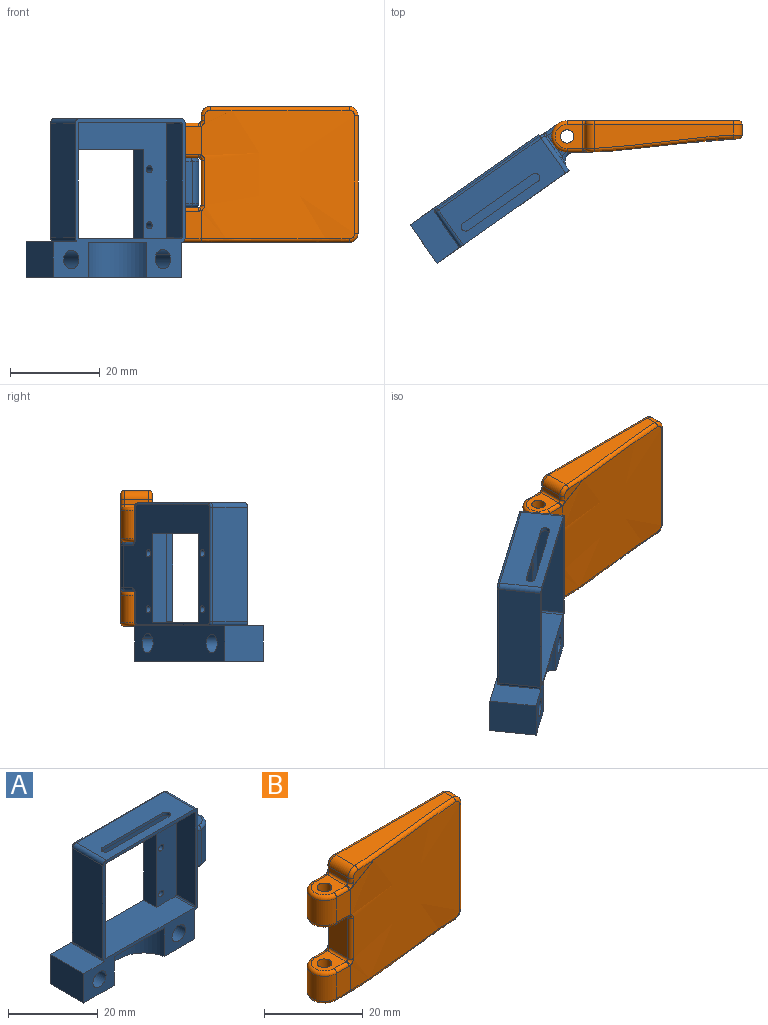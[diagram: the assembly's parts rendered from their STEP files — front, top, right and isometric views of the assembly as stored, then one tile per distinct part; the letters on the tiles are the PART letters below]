
ASSEMBLY  parts=2 mates=1
PART A: 71 faces, bbox 43.8x11x35.5 mm
  f0: plane 15.72x6.5mm, normal (0,0,-1), area 76.7mm2, adj f17,f61
  f1: plane 18x4mm, normal (0,0,-1), area 72mm2, adj f2,f7,f8,f9
  f2: plane 20x4mm, normal (-1,0,0), area 80mm2, adj f1,f8,f9,f13
  f3: cylinder r=0.8mm len=4mm, axis (0,1,0), area 20.1mm2, adj f8,f9
  f4: cylinder r=0.8mm len=4mm, axis (0,1,0), area 20.1mm2, adj f8,f9
  f5: cylinder r=0.8mm len=4mm, axis (0,1,0), area 20.1mm2, adj f8,f9
  f6: cylinder r=0.8mm len=4mm, axis (0,1,0), area 20.1mm2, adj f8,f9
  f7: plane 20x4mm, normal (1,0,0), area 80mm2, adj f1,f8,f9,f13
  f8: plane 28.3x26mm, normal (0,-1,0), area 367.7mm2, adj f1,f2,f3,f4,f5,f6,f7,f10
  f9: plane 33.4x26.6mm, normal (0,1,0), area 443.5mm2, adj f1,f2,f3,f4,f5,f6,f7,f13
  f10: plane 25.3x6mm, normal (-1,0,0), area 151.8mm2, adj f8,f17,f28,f29
  f11: plane 27.6x6mm, normal (0,0,-1), area 124.5mm2, adj f8,f17,f18,f19,f20,f21,f27,f28
  f12: plane 25.3x6mm, normal (1,0,0), area 151.8mm2, adj f8,f17,f26,f27
  f13: plane 27.6x10mm, normal (0,0,1), area 237.6mm2, adj f2,f7,f8,f9,f17,f26,f29
  f14: plane 25.6x9.5mm, normal (1,0,0), area 143.4mm2, adj f17,f22,f25,f35,f44,f45,f46,f47
  f15: plane 27.9x9.5mm, normal (0,0,1), area 223.9mm2, adj f17,f18,f19,f20,f21,f22,f23,f53
  f16: plane 25.6x9.5mm, normal (-1,0,0), area 243.2mm2, adj f17,f23,f24,f55
  f17: plane 35.98x35.43mm, normal (0,-1,0), area 213.2mm2, adj f0,f10,f11,f12,f13,f14,f15,f16
  f18: plane 19x0.8mm, normal (0,-1,0), area 15.2mm2, adj f11,f15,f20,f21
  f19: plane 19x0.8mm, normal (0,1,0), area 15.2mm2, adj f11,f15,f20,f21
  f20: cylinder r=1mm len=2mm, axis (0,0,-1), area 2.5mm2, adj f11,f15,f18,f19
  f21: cylinder r=1mm len=2mm, axis (0,0,1), area 2.5mm2, adj f11,f15,f18,f19
  f22: cylinder r=1mm len=9.5mm, axis (0,1,0), area 14.9mm2, adj f14,f15,f17,f52
  f23: cylinder r=1mm len=9.5mm, axis (0,-1,0), area 14.9mm2, adj f15,f16,f17,f54
  f24: cylinder r=1mm len=9.5mm, axis (0,1,0), area 9.3mm2, adj f16,f17,f56,f70
  f25: cylinder r=1mm len=9.5mm, axis (0,-1,0), area 14.7mm2, adj f14,f17,f58,f68
  f26: cylinder r=0.35mm len=6mm, axis (0,-1,0), area 3.3mm2, adj f8,f12,f13,f17
  f27: cylinder r=0.35mm len=6mm, axis (0,1,0), area 3.3mm2, adj f8,f11,f12,f17
  f28: cylinder r=0.35mm len=6mm, axis (0,-1,0), area 3.3mm2, adj f8,f10,f11,f17
  f29: cylinder r=0.35mm len=6mm, axis (0,1,0), area 3.3mm2, adj f8,f10,f13,f17
  f30: plane 9.4x2mm, normal (0,-1,0), area 18.8mm2, adj f31,f35,f37,f41
  f31: cylinder r=3.5mm len=9.4mm, axis (0,0,-1), area 103.4mm2, adj f9,f30,f38,f42
  f32: cylinder r=1.5mm len=11mm, axis (0,0,-1), area 103.7mm2, adj f33,f34
  f33: plane 6.2x5.84mm, normal (0,0,1), area 23.5mm2, adj f32,f40,f41,f42,f43,f45
  f34: plane 6.2x5.84mm, normal (0,0,-1), area 23.5mm2, adj f32,f36,f37,f38,f39,f48
  f35: cylinder r=2mm len=9.4mm, axis (0,0,1), area 29.5mm2, adj f14,f30,f36,f40
  f36: torus R=2.8mm, axis (0,0,1), area 2.7mm2, adj f34,f35,f37,f47
  f37: cylinder r=0.8mm len=2mm, axis (1,0,0), area 2.5mm2, adj f30,f34,f36,f38
  f38: torus R=2.7mm, axis (0,0,1), area 12.7mm2, adj f31,f34,f37,f39
  f39: cylinder r=0.8mm len=3.5mm, axis (-1,0,0), area 4.4mm2, adj f9,f34,f38,f49
  f40: torus R=2.8mm, axis (0,0,1), area 2.7mm2, adj f33,f35,f41,f44
  f41: cylinder r=0.8mm len=2mm, axis (-1,0,0), area 2.5mm2, adj f30,f33,f40,f42
  f42: torus R=2.7mm, axis (0,0,1), area 12.7mm2, adj f31,f33,f41,f43
  f43: cylinder r=0.8mm len=3.5mm, axis (1,0,0), area 4.4mm2, adj f9,f33,f42,f46
  f44: bspline ~2.36x1.3mm, area 1.1mm2, adj f14,f40,f45
  f45: cylinder r=0.5mm len=5.84mm, axis (0,1,0), area 4.6mm2, adj f14,f33,f44,f46
  f46: torus R=1.3mm, axis (1,0,0), area 0.5mm2, adj f14,f43,f45,f50
  f47: bspline ~2.73x1.3mm, area 1.1mm2, adj f14,f36,f48
  f48: cylinder r=0.5mm len=5.84mm, axis (0,-1,0), area 4.6mm2, adj f14,f34,f47,f49
  f49: torus R=1.3mm, axis (1,0,0), area 0.5mm2, adj f14,f39,f48,f60
  f50: bspline ~1.48x1mm, area 0.7mm2, adj f9,f46,f51
  f51: cylinder r=0.5mm len=7.34mm, axis (0,0,1), area 5.8mm2, adj f9,f14,f50,f52
  f52: torus R=0.5mm, axis (0,-1,0), area 1mm2, adj f9,f22,f51,f53
  f53: cylinder r=0.5mm len=27.9mm, axis (-1,0,0), area 21.9mm2, adj f9,f15,f52,f54
  f54: torus R=0.5mm, axis (0,-1,0), area 1mm2, adj f9,f23,f53,f55
  f55: cylinder r=0.5mm len=25.6mm, axis (0,0,-1), area 20.1mm2, adj f9,f16,f54,f56
  f56: torus R=0.5mm, axis (0,-1,0), area 0.8mm2, adj f9,f24,f55,f57,f70
  f57: cylinder r=0.5mm len=27.9mm, axis (1,0,0), area 10mm2, adj f9,f56,f58,f70
  f58: torus R=0.5mm, axis (0,-1,0), area 1mm2, adj f9,f25,f57,f59,f68,f70
  f59: cylinder r=0.5mm len=6.34mm, axis (0,0,1), area 5mm2, adj f9,f14,f58,f60
  f60: bspline ~1.48x1mm, area 0.7mm2, adj f9,f49,f59
  f61: cylinder r=8mm len=15.72mm, axis (0,0,1), area 173.1mm2, adj f0,f17,f67
  f62: cylinder r=2.09mm len=10.5mm, axis (0,-1,0), area 79.3mm2, adj f17,f63,f64
  f63: cylinder r=2.06mm len=10.5mm, axis (0,1,0), area 60.9mm2, adj f17,f62,f64
  f64: plane 35x8mm, normal (0,1,0), area 252.4mm2, adj f62,f63,f65,f66,f67,f68,f69,f70
  f65: cylinder r=2mm len=10.5mm, axis (0,1,0), area 37mm2, adj f17,f64,f66
  f66: cylinder r=2.06mm len=10.5mm, axis (0,1,0), area 99.4mm2, adj f17,f64,f65
  f67: plane 35x10.5mm, normal (0,0,-1), area 290.8mm2, adj f17,f61,f64,f68,f69
  f68: plane 10.5x8mm, normal (1,0,0), area 82.3mm2, adj f17,f25,f58,f64,f67,f70
  f69: plane 10.5x8mm, normal (-1,0,0), area 84mm2, adj f17,f64,f67,f70
  f70: plane 35x10.5mm, normal (0,0,1), area 86.3mm2, adj f17,f24,f56,f57,f58,f64,f68,f69
PART B: 58 faces, bbox 43x7.6x30.6 mm
  f0: plane 6.28x4mm, normal (0,-1,0), area 24.7mm2, adj f3,f10,f34,f35,f39
  f1: cylinder r=1.5mm len=7.78mm, axis (0,0,-1), area 73.3mm2, adj f8,f15
  f2: plane 38.2x28.7mm, normal (0,1,0), area 1018mm2, adj f3,f4,f22,f24,f26,f28,f30,f36
  f3: cylinder r=3.5mm len=7mm, axis (0,0,-1), area 67.9mm2, adj f0,f2,f32,f37
  f4: cylinder r=3.5mm len=7mm, axis (0,0,-1), area 67.9mm2, adj f2,f5,f23,f54
  f5: plane 6.38x4mm, normal (0,-1,0), area 24.7mm2, adj f4,f10,f25,f27,f56,f57
  f6: cylinder r=1.5mm len=7.78mm, axis (0,0,-1), area 73.3mm2, adj f7,f14
  f7: plane 6.2x5.4mm, normal (0,0,1), area 23.3mm2, adj f6,f18,f52,f54,f56
  f8: plane 39.7x5.4mm, normal (0,0,-1), area 157.5mm2, adj f1,f19,f36,f37,f39,f41
  f9: plane 5.4x1.2mm, normal (-1,0,0), area 6.5mm2, adj f18,f20,f48,f53
  f10: extruded ~34.21x28.7mm, area 972.4mm2, adj f0,f5,f29,f31,f33,f41,f43,f45
  f11: plane 26.3x2.4mm, normal (1,0,0), area 63.2mm2, adj f19,f21,f40,f45
  f12: plane 31x5.37mm, normal (0,0,1), area 120.8mm2, adj f20,f21,f44,f49
  f13: plane 10.05x5.4mm, normal (-1,0,0), area 54.2mm2, adj f16,f17,f26,f31
  f14: plane 6.2x5.4mm, normal (0,0,-1), area 23.3mm2, adj f6,f17,f22,f23,f25
  f15: plane 6.2x5.4mm, normal (0,0,1), area 23.3mm2, adj f1,f16,f30,f32,f34
  f16: cylinder r=0.5mm len=5.4mm, axis (0,-1,0), area 4.2mm2, adj f13,f15,f28,f33,f35
  f17: cylinder r=0.5mm len=5.4mm, axis (0,1,0), area 4.2mm2, adj f13,f14,f24,f27,f29
  f18: cylinder r=0.5mm len=5.4mm, axis (0,1,0), area 4.2mm2, adj f7,f9,f50,f55,f57
  f19: cylinder r=2mm len=2.43mm, axis (0,1,0), area 7.6mm2, adj f8,f11,f38,f43
  f20: cylinder r=2mm len=5.4mm, axis (0,1,0), area 16.9mm2, adj f9,f12,f46,f51
  f21: cylinder r=2mm len=2.43mm, axis (0,-1,0), area 7.6mm2, adj f11,f12,f42,f47
  f22: cylinder r=0.8mm len=3.5mm, axis (-1,0,0), area 4.4mm2, adj f2,f14,f23,f24
  f23: torus R=2.7mm, axis (0,0,1), area 12.7mm2, adj f4,f14,f22,f25
  f24: torus R=1.3mm, axis (0,1,0), area 1.6mm2, adj f2,f17,f22,f26
  f25: cylinder r=0.8mm len=3.5mm, axis (1,0,0), area 4.4mm2, adj f5,f14,f23,f27
  f26: cylinder r=0.8mm len=10.05mm, axis (0,0,-1), area 12.6mm2, adj f2,f13,f24,f28
  f27: torus R=1.3mm, axis (0,1,0), area 0.4mm2, adj f5,f17,f25,f29
  f28: torus R=1.3mm, axis (0,1,0), area 1.6mm2, adj f2,f16,f26,f30
  f29: bspline ~1.41x1.15mm, area 1.2mm2, adj f10,f17,f27,f31
  f30: cylinder r=0.8mm len=3.5mm, axis (1,0,0), area 4.4mm2, adj f2,f15,f28,f32
  f31: cylinder r=0.8mm len=10.05mm, axis (0,0,-1), area 12.7mm2, adj f10,f13,f29,f33
  f32: torus R=2.7mm, axis (0,0,1), area 12.7mm2, adj f3,f15,f30,f34
  f33: bspline ~1.41x1.15mm, area 1.2mm2, adj f10,f16,f31,f35
  f34: cylinder r=0.8mm len=3.5mm, axis (-1,0,0), area 4.4mm2, adj f0,f15,f32,f35
  f35: torus R=1.3mm, axis (0,1,0), area 0.4mm2, adj f0,f16,f33,f34
  f36: cylinder r=0.8mm len=37mm, axis (-1,0,0), area 46.5mm2, adj f2,f8,f37,f38
  f37: torus R=2.7mm, axis (0,0,1), area 12.7mm2, adj f3,f8,f36,f39
  f38: torus R=1.2mm, axis (0,1,0), area 3.4mm2, adj f2,f19,f36,f40
  f39: cylinder r=0.8mm len=4mm, axis (1,0,0), area 5mm2, adj f0,f8,f37,f41
  f40: cylinder r=0.8mm len=26.3mm, axis (0,0,-1), area 33mm2, adj f2,f11,f38,f42
  f41: bspline ~41.04x3.79mm, area 41.7mm2, adj f8,f10,f39,f43
  f42: torus R=1.2mm, axis (0,1,0), area 3.4mm2, adj f2,f21,f40,f44
  f43: bspline ~2.45x2.45mm, area 3.3mm2, adj f10,f19,f41,f45
  f44: cylinder r=0.8mm len=31mm, axis (1,0,0), area 39mm2, adj f2,f12,f42,f46
  f45: cylinder r=0.8mm len=26.3mm, axis (0,0,-1), area 32.8mm2, adj f10,f11,f43,f47
  f46: torus R=1.2mm, axis (0,1,0), area 3.4mm2, adj f2,f20,f44,f48
  f47: bspline ~2.45x2.45mm, area 3.3mm2, adj f10,f21,f45,f49
  f48: cylinder r=0.8mm len=1.2mm, axis (0,0,1), area 1.5mm2, adj f2,f9,f46,f50
  f49: bspline ~32.8x3.78mm, area 39.1mm2, adj f10,f12,f47,f51
  f50: torus R=1.3mm, axis (0,1,0), area 1.6mm2, adj f2,f18,f48,f52
  f51: bspline ~2.47x2.45mm, area 3.4mm2, adj f10,f20,f49,f53
  f52: cylinder r=0.8mm len=3.5mm, axis (1,0,0), area 4.4mm2, adj f2,f7,f50,f54
  f53: cylinder r=0.8mm len=1.2mm, axis (0,0,-1), area 1.5mm2, adj f9,f10,f51,f55
  f54: torus R=2.7mm, axis (0,0,1), area 12.7mm2, adj f4,f7,f52,f56
  f55: bspline ~1.41x1.15mm, area 1.2mm2, adj f10,f18,f53,f57
  f56: cylinder r=0.8mm len=3.5mm, axis (-1,0,0), area 4.4mm2, adj f5,f7,f54,f57
  f57: torus R=1.3mm, axis (0,1,0), area 0.4mm2, adj f5,f18,f55,f56
PLACE A rot(axis=(0,0,1),35deg) t=(-33.12,-19.62,-12.5)mm
PLACE B at identity fixed
MATE revolute A.f31 <-> B.f1  axis (0,0,-1) through (-4,-3.5,0)mm
